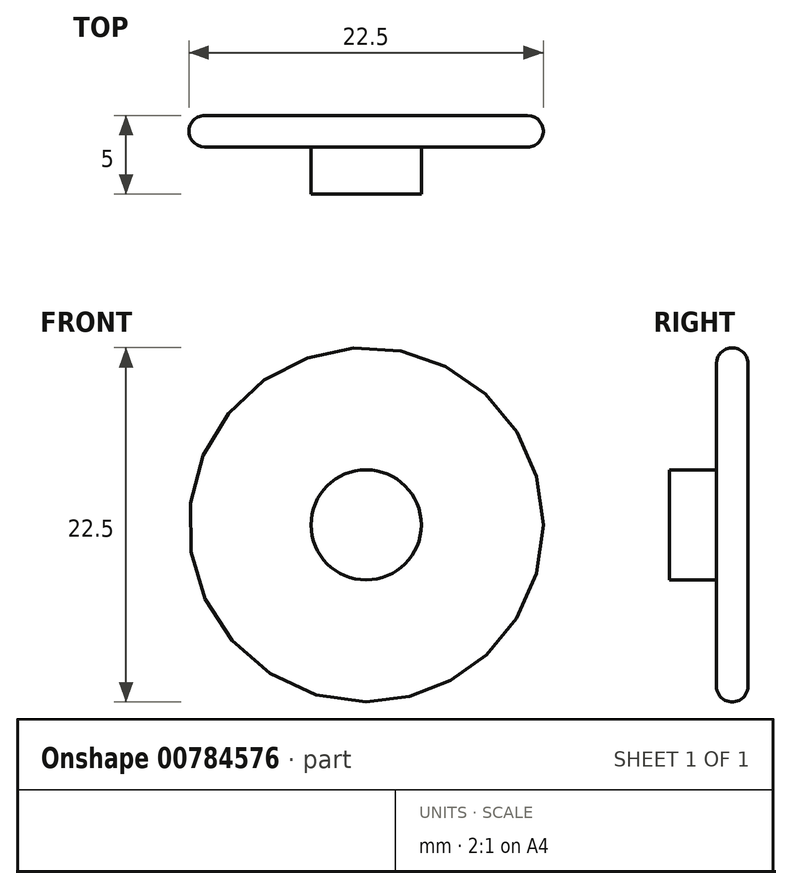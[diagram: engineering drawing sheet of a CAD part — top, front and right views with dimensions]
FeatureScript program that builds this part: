
annotation { "Feature Type Name" : "Feature", "Feature Type Description" : "" }
export const myFeature = defineFeature(function(context is Context, id is Id, definition is map)
    precondition{}
    {
        {
            var Q0;
            Q0=qCreatedBy(makeId("Front.planeOp"),FACE);
            var sketch = newSketch(context, id + "F0", { "sketchPlane" : qUnion([Q0])});
            skCircle(sketch, "E0", {"center": v(0, 0) * mm, "radius": 11.25 * mm});
            skCircle(sketch, "E1", {"center": v(0, 0) * mm, "radius": 3.5 * mm});
            skSolve(sketch);
        }
        {
            var Q0;
            Q0=makeQuery(id+"F0.imprint","IMPRINT",FACE,{"disambiguationData":[TD([[makeQuery(id+"F0.imprint","IMPRINT",EDGE,{"derivedFrom":sQuery(id+"F0.wireOp",EDGE,"E1")}),1.0]])]});
            extrude(context, id + "F1", {"entities" : qUnion([Q0]), "depth" : 5 * mm, "offsetDistance" : 25.4 * mm});
        }
        {
            var Q0;
            Q0 = qSketchRegion(id + "F0", true);
            extrude(context, id + "F2", {"entities" : qUnion([Q0]), "operationType" : NewBodyOperationType.ADD, "depth" : 2 * mm, "offsetDistance" : 25.4 * mm});
        }
        {
            var Q0;
            Q0=makeQuery(id+"F2.opExtrude","CAP_EDGE",EDGE,{"disambiguationData":[OSD([sQuery(id+"F0.wireOp",EDGE,"E0")])],"isStart":false});
            var Q1;
            Q1=makeQuery(id+"F2.opExtrude","CAP_EDGE",EDGE,{"disambiguationData":[OSD([sQuery(id+"F0.wireOp",EDGE,"E0")])],"isStart":true});
            fillet(context, id + "F3", {"entities" : qUnion([Q0, Q1]), "radius" : 1 * mm, "tangentPropagation" : true, "allowEdgeOverflow" : false});
        }
    });
